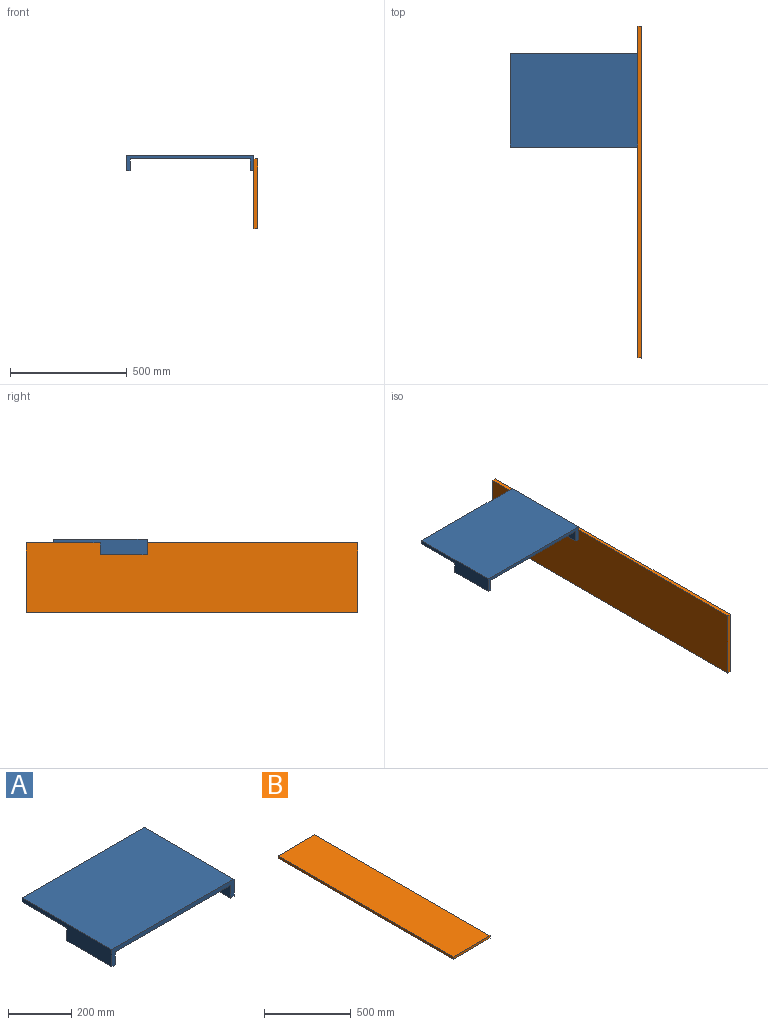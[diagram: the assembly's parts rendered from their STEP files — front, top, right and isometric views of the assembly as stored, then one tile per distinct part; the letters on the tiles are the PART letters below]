
ASSEMBLY  parts=2 mates=1
PART A: 12 faces, bbox 548x403x66 mm
  f0: plane 403x66mm, normal (1,0,0), area 16523mm2, adj f1,f3,f4,f5,f6,f8
  f1: plane 548x16mm, normal (0,1,0), area 8768mm2, adj f0,f2,f4,f5
  f2: plane 403x66mm, normal (-1,0,0), area 16523mm2, adj f1,f3,f4,f5,f9,f11
  f3: plane 548x66mm, normal (0,-1,0), area 10368mm2, adj f0,f2,f4,f5,f7,f8,f10,f11
  f4: plane 548x403mm, normal (0,0,1), area 220844mm2, adj f0,f1,f2,f3
  f5: plane 548x403mm, normal (0,0,-1), area 214396mm2, adj f0,f1,f2,f3,f6,f7,f9,f10
  f6: plane 50x16mm, normal (0,1,0), area 800mm2, adj f0,f5,f7,f8
  f7: plane 201.5x50mm, normal (-1,0,0), area 10075mm2, adj f3,f5,f6,f8
  f8: plane 201.5x16mm, normal (0,0,-1), area 3224mm2, adj f0,f3,f6,f7
  f9: plane 50x16mm, normal (0,1,0), area 800mm2, adj f2,f5,f10,f11
  f10: plane 201.5x50mm, normal (1,0,0), area 10075mm2, adj f3,f5,f9,f11
  f11: plane 201.5x16mm, normal (0,0,-1), area 3224mm2, adj f2,f3,f9,f10
PART B: 6 faces, bbox 300x1424x16 mm
  f0: plane 1424x16mm, normal (-1,0,0), area 22784mm2, adj f1,f3,f4,f5
  f1: plane 300x16mm, normal (0,-1,0), area 4800mm2, adj f0,f2,f4,f5
  f2: plane 1424x16mm, normal (1,0,0), area 22784mm2, adj f1,f3,f4,f5
  f3: plane 300x16mm, normal (0,1,0), area 4800mm2, adj f0,f2,f4,f5
  f4: plane 1424x300mm, normal (0,0,1), area 427200mm2, adj f0,f1,f2,f3
  f5: plane 1424x300mm, normal (0,0,-1), area 427200mm2, adj f0,f1,f2,f3
PLACE A t=(745.91,-599.41,-317.43)mm
PLACE B rot(axis=(0,1,0),90deg) t=(446.07,-560.17,-508.87)mm
MATE revolute A.f0 <-> B.f5  axis (-1,0,0) through (446.07,308.45,-367.43)mm
